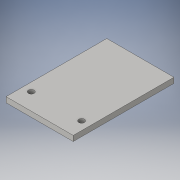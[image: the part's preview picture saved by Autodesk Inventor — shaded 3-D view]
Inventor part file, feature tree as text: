
AUTODESK INVENTOR PART (.ipt)
format: ipt  version: 2016 (Build 200138000, 138)  size: 99,328 bytes
history: native  units: in
note: dims shown in document units (in); Inventor stores cm internally (conversion verified against a paired STEP export)
features: sketch x2, extrude x1, hole x1
ambient origin geometry x8: Origin, YZ Plane, XZ Plane, XY Plane, X Axis, Y Axis, Z Axis, Center Point
bodies: Solid1 (feature_tree)
feature tree (4):
  extrude  "Extrusion1"  Depth=2.0in
  hole  "Hole1"  [1 undecoded]
  sketch  "Sketch1"  dims[d0=3.0in d1=2.0in]
  sketch  "Sketch2"  dims[d2=1.0in d3=1.5in d4=0.1575in d5=0.0in d6=0.5in d7=0.5in d8=1.5in d9=0.25in d10=0.1695in d11=0.75in d12=0.375in d13=0.25in d14=0.5635in d15=1.0in d16=0.8108in]
note: 1 required parameter value undecoded (feature->parameter linkage not recoverable at this tier; creation-order binding heuristic only, values carry confidence <= 0.55)
